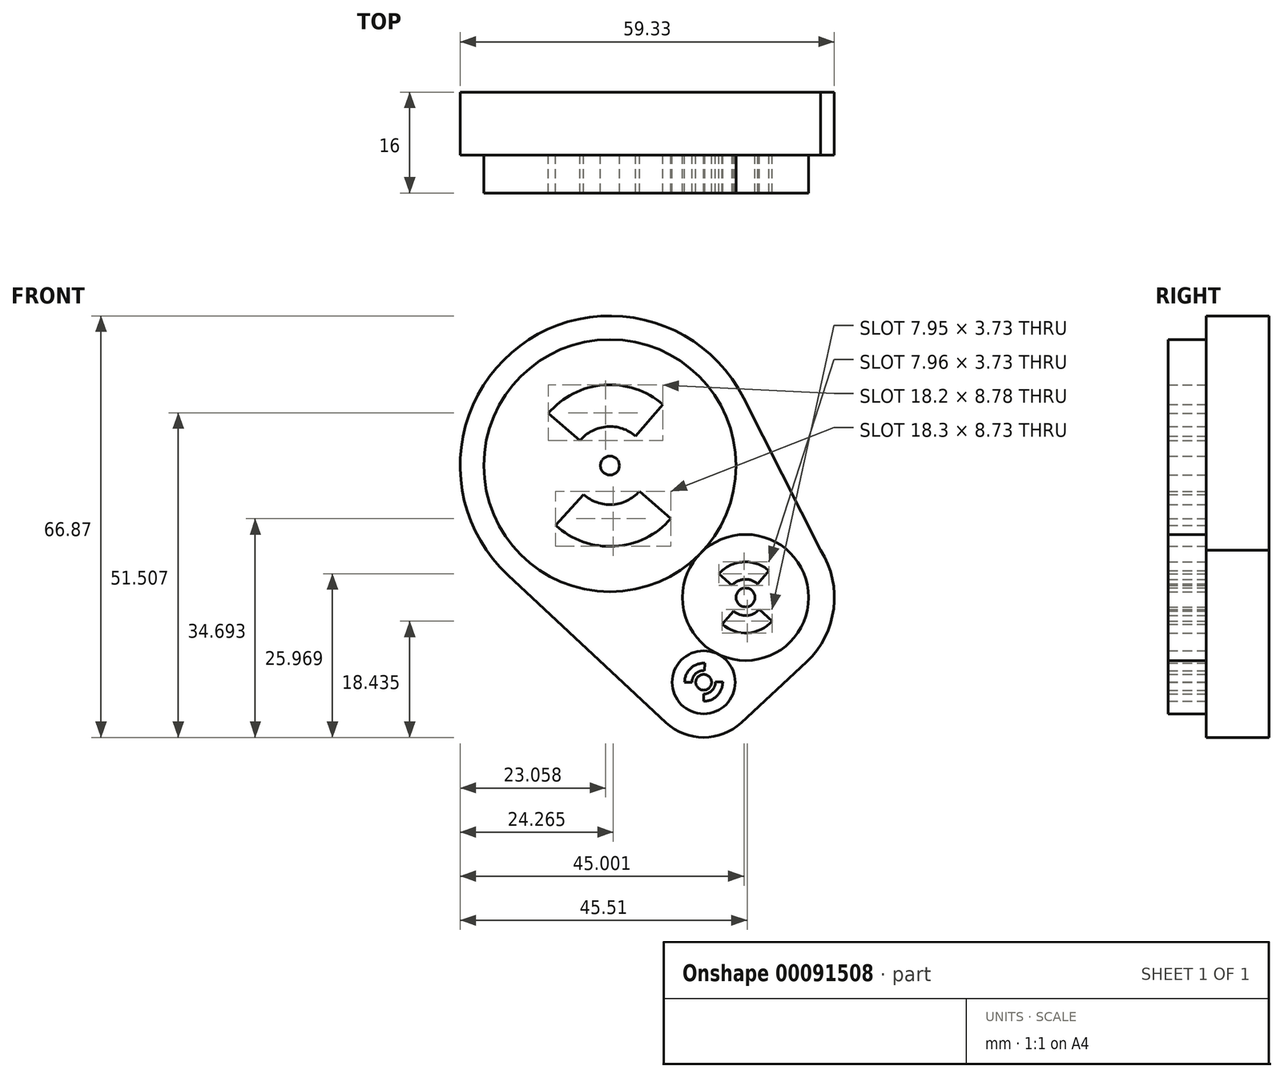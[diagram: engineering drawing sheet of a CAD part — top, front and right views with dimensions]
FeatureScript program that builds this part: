
annotation { "Feature Type Name" : "Feature", "Feature Type Description" : "" }
export const myFeature = defineFeature(function(context is Context, id is Id, definition is map)
    precondition{}
    {
        {
            var Q0;
            Q0=qCreatedBy(makeId("Front.planeOp"),FACE);
            var sketch = newSketch(context, id + "F0", { "sketchPlane" : qUnion([Q0])});
            skCircle(sketch, "E0", {"center": v(17.86, 15.02) * mm, "radius": 10 * mm});
            skCircle(sketch, "E1", {"center": v(11.22, 1.57) * mm, "radius": 5 * mm});
            skCircle(sketch, "E2", {"center": v(-3.64, 35.94) * mm, "radius": 20 * mm});
            skCircle(sketch, "E3", {"center": v(-3.64, 35.94) * mm, "radius": 1.5 * mm});
            skCircle(sketch, "E4", {"center": v(17.86, 15.02) * mm, "radius": 1.5 * mm});
            skCircle(sketch, "E5", {"center": v(11.22, 1.57) * mm, "radius": 1.25 * mm});
            skArc(sketch, "E6", {"start": v(17.55, 46.67) * mm, "mid": v(-17.91, 54.93) * mm, "end": v(-19.84, 18.57) * mm});
            skArc(sketch, "E7", {"start": v(5.26, -4.83) * mm, "mid": v(11.22, -7.18) * mm, "end": v(17.18, -4.84) * mm});
            skLineSegment(sketch, "E8", {"start": v(17.55, 46.67) * mm, "end": v(29.78, 22.51) * mm});
            skLineSegment(sketch, "E9", {"start": v(27.54, 4.8) * mm, "end": v(17.18, -4.84) * mm});
            skLineSegment(sketch, "E10", {"start": v(-19.84, 18.57) * mm, "end": v(5.26, -4.83) * mm});
            skArc(sketch, "E11.trimOffspring", {"start": v(27.54, 4.8) * mm, "mid": v(31.83, 13.25) * mm, "end": v(29.78, 22.51) * mm});
            skLineSegment(sketch, "E12", {"start": v(-10.2, 9.6) * mm, "end": v(-7.15, 12.87) * mm});
            skLineSegment(sketch, "E13", {"start": v(-7.15, 12.87) * mm, "end": v(3.24, 12.87) * mm});
            skLineSegment(sketch, "E14", {"start": v(3.24, 12.87) * mm, "end": v(3.24, 0) * mm});
            skLineSegment(sketch, "E15", {"start": v(3.24, 0) * mm, "end": v(1.77, -1.58) * mm});
            skLineSegment(sketch, "E16", {"start": v(20.87, 40.33) * mm, "end": v(20.78, 40.29) * mm});
            skLineSegment(sketch, "E17", {"start": v(20.87, 40.33) * mm, "end": v(20.87, 28.54) * mm});
            skLineSegment(sketch, "E18", {"start": v(20.87, 28.54) * mm, "end": v(28.36, 25.33) * mm});
            skArc(sketch, "E19", {"start": v(-12.28, 26.47) * mm, "mid": v(-2.9, 23.15) * mm, "end": v(6.03, 27.53) * mm});
            skArc(sketch, "E20", {"start": v(-7.81, 31.37) * mm, "mid": v(-3.28, 29.76) * mm, "end": v(1.03, 31.88) * mm});
            skLineSegment(sketch, "E21", {"start": v(-12.28, 26.47) * mm, "end": v(-7.81, 31.37) * mm});
            skLineSegment(sketch, "E22", {"start": v(-13.43, 44.21) * mm, "end": v(-8.37, 39.94) * mm});
            skLineSegment(sketch, "E23.trimOffspring", {"start": v(0.42, 40.61) * mm, "end": v(4.77, 45.61) * mm});
            skLineSegment(sketch, "E24.trimOffspring", {"start": v(1.03, 31.88) * mm, "end": v(6.03, 27.53) * mm});
            skArc(sketch, "E25.trimOffspring", {"start": v(0.42, 40.61) * mm, "mid": v(-4.12, 42.11) * mm, "end": v(-8.37, 39.94) * mm});
            skArc(sketch, "E26.trimOffspring", {"start": v(4.77, 45.61) * mm, "mid": v(-4.62, 48.72) * mm, "end": v(-13.43, 44.21) * mm});
            skArc(sketch, "E27", {"start": v(14.15, 10.78) * mm, "mid": v(18.23, 9.4) * mm, "end": v(22.1, 11.3) * mm});
            skLineSegment(sketch, "E28", {"start": v(14.15, 10.78) * mm, "end": v(15.97, 12.86) * mm});
            skLineSegment(sketch, "E29", {"start": v(19.77, 17.18) * mm, "end": v(21.6, 19.25) * mm});
            skLineSegment(sketch, "E30", {"start": v(13.63, 18.75) * mm, "end": v(15.7, 16.93) * mm});
            skLineSegment(sketch, "E31", {"start": v(20.02, 13.12) * mm, "end": v(22.1, 11.3) * mm});
            skArc(sketch, "E32", {"start": v(15.97, 12.86) * mm, "mid": v(18.05, 12.15) * mm, "end": v(20.02, 13.12) * mm});
            skArc(sketch, "E33.trimOffspring", {"start": v(19.77, 17.18) * mm, "mid": v(17.68, 17.9) * mm, "end": v(15.7, 16.93) * mm});
            skArc(sketch, "E34.trimOffspring", {"start": v(21.6, 19.25) * mm, "mid": v(17.5, 20.65) * mm, "end": v(13.63, 18.75) * mm});
            skArc(sketch, "E35", {"start": v(11.22, -1.45) * mm, "mid": v(13.39, -0.54) * mm, "end": v(14.24, 1.66) * mm});
            skArc(sketch, "E36", {"start": v(11.35, 3.43) * mm, "mid": v(9.95, 2.93) * mm, "end": v(9.36, 1.57) * mm});
            skLineSegment(sketch, "E37", {"start": v(11.43, 4.59) * mm, "end": v(11.35, 3.43) * mm});
            skLineSegment(sketch, "E38", {"start": v(11.22, -0.3) * mm, "end": v(11.22, -1.45) * mm});
            skLineSegment(sketch, "E39", {"start": v(11.22, -1.45) * mm, "end": v(11.22, -0.3) * mm});
            skLineSegment(sketch, "E40", {"start": v(14.24, 1.66) * mm, "end": v(13.09, 1.62) * mm});
            skLineSegment(sketch, "E41", {"start": v(9.36, 1.57) * mm, "end": v(8.2, 1.57) * mm});
            skArc(sketch, "E42.trimOffspring", {"start": v(11.43, 4.59) * mm, "mid": v(9.16, 3.78) * mm, "end": v(8.2, 1.57) * mm});
            skArc(sketch, "E43.trimOffspring", {"start": v(11.22, -0.3) * mm, "mid": v(12.56, 0.27) * mm, "end": v(13.09, 1.62) * mm});
            skPoint(sketch, "E44.endSnap0", {"position": v(11.22, -7.18) * mm});
            skSolve(sketch);
        }
        {
            var Q0;
            Q0=makeQuery(id+"F0.imprint","IMPRINT",FACE,{"disambiguationData":[TD([[makeQuery(id+"F0.imprint","IMPRINT",EDGE,{"derivedFrom":sQuery(id+"F0.wireOp",EDGE,"E2")}),1.0]])]});
            var Q1;
            Q1=makeQuery(id+"F0.imprint","IMPRINT",FACE,{"disambiguationData":[TD([[makeQuery(id+"F0.imprint","IMPRINT",EDGE,{"derivedFrom":sQuery(id+"F0.wireOp",EDGE,"E4")}),-1.0]])]});
            var Q2;
            Q2=makeQuery(id+"F0.imprint","IMPRINT",FACE,{"disambiguationData":[TD([[makeQuery(id+"F0.imprint","IMPRINT",EDGE,{"derivedFrom":sQuery(id+"F0.wireOp",EDGE,"E1")}),1.0]])]});
            extrude(context, id + "F1", {"entities" : qUnion([Q0, Q1, Q2]), "depth" : 6 * mm});
        }
        {
            var Q0;
            {var subQ5=sQuery(id+"F0.wireOp",EDGE,"E1");Q0=makeQuery(id+"F0.imprint","IMPRINT",FACE,{"disambiguationData":[TD([[makeQuery(id+"F0.imprint","IMPRINT",EDGE,{"derivedFrom":subQ5}),-1.0]])]});}
            var Q1;
            Q1=makeQuery(id+"F0.imprint","IMPRINT",FACE,{"disambiguationData":[TD([[makeQuery(id+"F0.imprint","IMPRINT",EDGE,{"derivedFrom":sQuery(id+"F0.wireOp",EDGE,"E27")}),1.0]])]});
            var Q2;
            Q2=makeQuery(id+"F0.imprint","IMPRINT",FACE,{"disambiguationData":[TD([[makeQuery(id+"F0.imprint","IMPRINT",EDGE,{"derivedFrom":sQuery(id+"F0.wireOp",EDGE,"E29")}),1.0]])]});
            var Q3;
            Q3=makeQuery(id+"F0.imprint","IMPRINT",FACE,{"disambiguationData":[TD([[makeQuery(id+"F0.imprint","IMPRINT",EDGE,{"derivedFrom":sQuery(id+"F0.wireOp",EDGE,"E4")}),1.0]])]});
            var Q4;
            Q4=makeQuery(id+"F0.imprint","IMPRINT",FACE,{"disambiguationData":[TD([[makeQuery(id+"F0.imprint","IMPRINT",EDGE,{"derivedFrom":sQuery(id+"F0.wireOp",EDGE,"E4")}),-1.0]])]});
            var Q5;
            {var subQ0=sQuery(id+"F0.wireOp",EDGE,"E12");Q5=makeQuery(id+"F0.imprint","IMPRINT",FACE,{"disambiguationData":[TD([[makeQuery(id+"F0.imprint","IMPRINT",EDGE,{"derivedFrom":subQ0}),-1.0]])]});}
            var Q6;
            Q6=makeQuery(id+"F0.imprint","IMPRINT",FACE,{"disambiguationData":[TD([[makeQuery(id+"F0.imprint","IMPRINT",EDGE,{"derivedFrom":sQuery(id+"F0.wireOp",EDGE,"E1")}),1.0]])]});
            var Q7;
            Q7=makeQuery(id+"F0.imprint","IMPRINT",FACE,{"disambiguationData":[TD([[makeQuery(id+"F0.imprint","IMPRINT",EDGE,{"derivedFrom":sQuery(id+"F0.wireOp",EDGE,"E36")}),-1.0]])]});
            var Q8;
            Q8=makeQuery(id+"F0.imprint","IMPRINT",FACE,{"disambiguationData":[TD([[makeQuery(id+"F0.imprint","IMPRINT",EDGE,{"derivedFrom":sQuery(id+"F0.wireOp",EDGE,"E35")}),1.0]])]});
            var Q9;
            {var subQ0=sQuery(id+"F0.wireOp",EDGE,"E18");Q9=makeQuery(id+"F0.imprint","IMPRINT",FACE,{"disambiguationData":[TD([[makeQuery(id+"F0.imprint","IMPRINT",EDGE,{"derivedFrom":subQ0}),1.0]])]});}
            var Q10;
            Q10=makeQuery(id+"F0.imprint","IMPRINT",FACE,{"disambiguationData":[TD([[makeQuery(id+"F0.imprint","IMPRINT",EDGE,{"derivedFrom":sQuery(id+"F0.wireOp",EDGE,"E5")}),1.0]])]});
            var Q11;
            Q11=makeQuery(id+"F0.imprint","IMPRINT",FACE,{"disambiguationData":[TD([[makeQuery(id+"F0.imprint","IMPRINT",EDGE,{"derivedFrom":sQuery(id+"F0.wireOp",EDGE,"E2")}),1.0]])]});
            var Q12;
            Q12=makeQuery(id+"F0.imprint","IMPRINT",FACE,{"disambiguationData":[TD([[makeQuery(id+"F0.imprint","IMPRINT",EDGE,{"derivedFrom":sQuery(id+"F0.wireOp",EDGE,"E19")}),1.0]])]});
            var Q13;
            Q13=makeQuery(id+"F0.imprint","IMPRINT",FACE,{"disambiguationData":[TD([[makeQuery(id+"F0.imprint","IMPRINT",EDGE,{"derivedFrom":sQuery(id+"F0.wireOp",EDGE,"E22")}),1.0]])]});
            var Q14;
            Q14=makeQuery(id+"F0.imprint","IMPRINT",FACE,{"disambiguationData":[TD([[makeQuery(id+"F0.imprint","IMPRINT",EDGE,{"derivedFrom":sQuery(id+"F0.wireOp",EDGE,"E3")}),1.0]])]});
            extrude(context, id + "F2", {"entities" : qUnion([Q0, Q1, Q2, Q3, Q4, Q5, Q6, Q7, Q8, Q9, Q10, Q11, Q12, Q13, Q14]), "oppositeDirection" : true, "depth" : 10 * mm});
        }
    });
